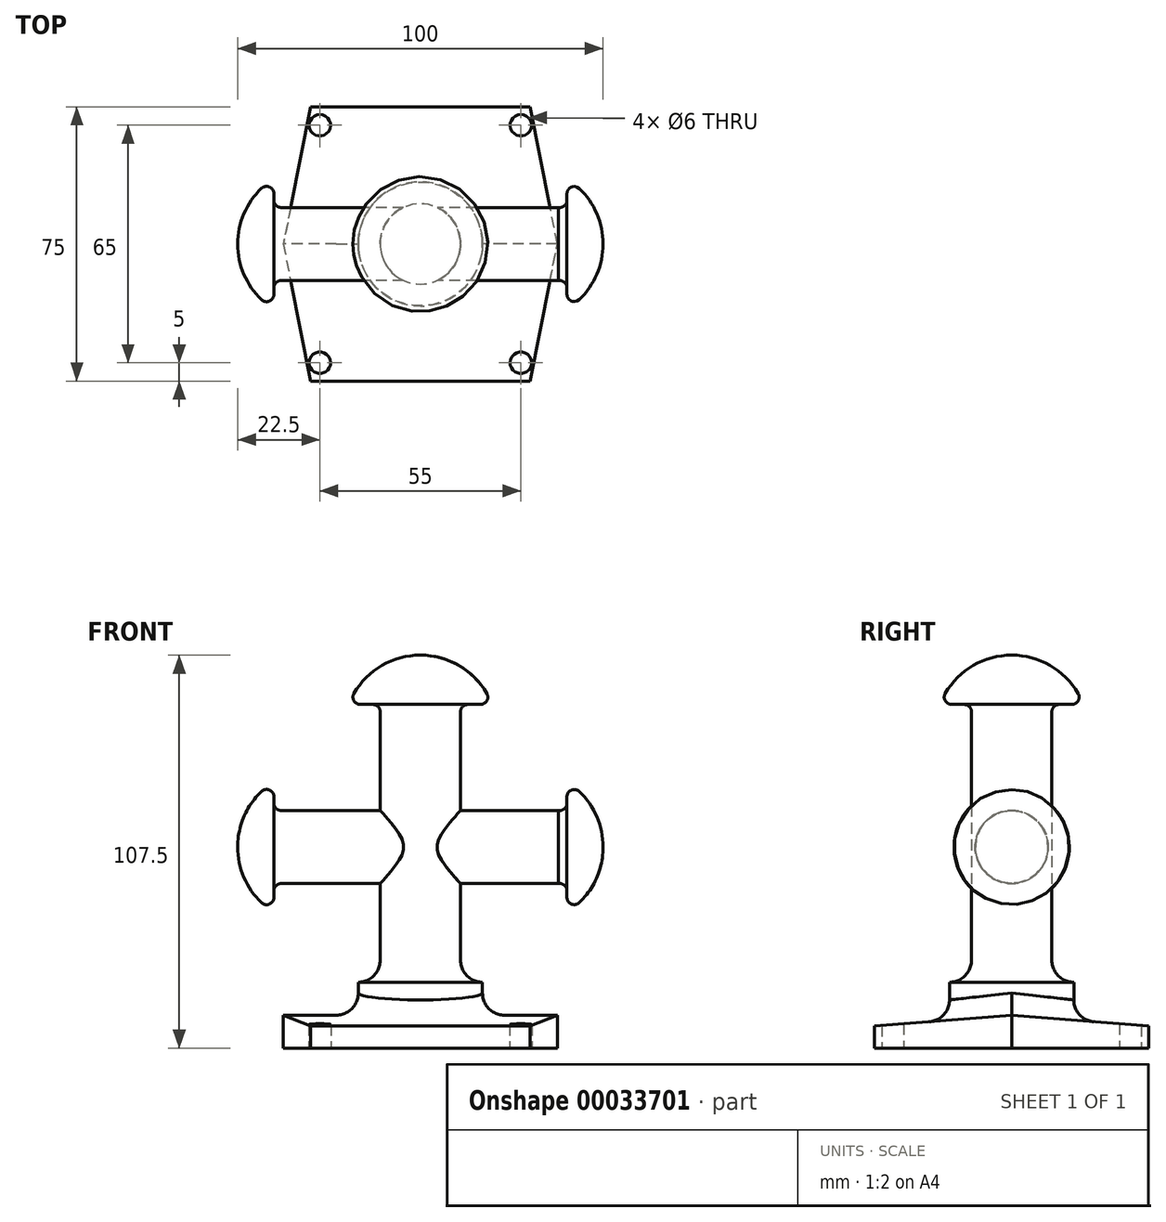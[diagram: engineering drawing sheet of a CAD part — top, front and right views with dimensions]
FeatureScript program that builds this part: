
annotation { "Feature Type Name" : "Feature", "Feature Type Description" : "" }
export const myFeature = defineFeature(function(context is Context, id is Id, definition is map)
    precondition{}
    {
        {
            var Q0;
            Q0=qCreatedBy(makeId("Front.planeOp"),FACE);
            var sketch = newSketch(context, id + "F0", { "sketchPlane" : qUnion([Q0])});
            skLineSegment(sketch, "E0", {"start": v(-38.09, 65) * mm, "end": v(37.8, 65) * mm});
            skLineSegment(sketch, "E1", {"start": v(-40.09, 67) * mm, "end": v(-40.09, 68.77) * mm});
            skArc(sketch, "E2", {"start": v(-43.47, 70.22) * mm, "mid": v(-48.3, 63.28) * mm, "end": v(-50, 55) * mm});
            skPoint(sketch, "E3.visualSharp", {"position": v(-40.09, 72.83) * mm});
            skArc(sketch, "E3.filletArc", {"start": v(-40.09, 68.77) * mm, "mid": v(-41.3, 70.61) * mm, "end": v(-43.47, 70.22) * mm});
            skPoint(sketch, "E4.visualSharp", {"position": v(-40.09, 65) * mm});
            skArc(sketch, "E4.filletArc", {"start": v(-40.09, 67) * mm, "mid": v(-39.5, 65.59) * mm, "end": v(-38.09, 65) * mm});
            skLineSegment(sketch, "E5", {"start": v(-29, 55) * mm, "end": v(29, 55) * mm});
            skLineSegment(sketch, "E6", {"start": v(0, 0) * mm, "end": v(0, 55) * mm, "construction": true});
            skArc(sketch, "E7", {"start": v(50, 55) * mm, "mid": v(48.3, 63.26) * mm, "end": v(43.5, 70.2) * mm});
            skArc(sketch, "E8", {"start": v(43.5, 70.2) * mm, "mid": v(41.33, 70.59) * mm, "end": v(40.12, 68.75) * mm});
            skLineSegment(sketch, "E9", {"start": v(40.12, 68.75) * mm, "end": v(40.12, 66.98) * mm});
            skArc(sketch, "E10", {"start": v(40.12, 66.98) * mm, "mid": v(39.41, 65.45) * mm, "end": v(37.8, 65) * mm});
            skLineSegment(sketch, "E11", {"start": v(-29, 55) * mm, "end": v(-50, 55) * mm});
            skLineSegment(sketch, "E12", {"start": v(29, 55) * mm, "end": v(50, 55) * mm});
            skSolve(sketch);
        }
        {
            var Q0;
            Q0 = qSketchRegion(id + "F0", true);
            var Q1;
            Q1=sQuery(id+"F0.wireOp",EDGE,"E5");
            revolve(context, id + "F1", {"entities" : qUnion([Q0]), "axis" : qUnion([Q1]), "revolveType" : RevolveType.FULL});
        }
        {
            var Q0;
            Q0=qCreatedBy(makeId("Front.planeOp"),FACE);
            var sketch = newSketch(context, id + "F2", { "sketchPlane" : qUnion([Q0])});
            skLineSegment(sketch, "E13", {"start": v(16.45, 94) * mm, "end": v(13, 94) * mm});
            skLineSegment(sketch, "E14", {"start": v(11, 92) * mm, "end": v(11, 18) * mm});
            skArc(sketch, "E15", {"start": v(18.19, 97) * mm, "mid": v(10.5, 104.69) * mm, "end": v(0, 107.5) * mm});
            skPoint(sketch, "E16.visualSharp", {"position": v(19.62, 94) * mm});
            skArc(sketch, "E16.filletArc", {"start": v(16.45, 94) * mm, "mid": v(18.19, 95) * mm, "end": v(18.19, 97) * mm});
            skPoint(sketch, "E17.visualSharp", {"position": v(11, 94) * mm});
            skArc(sketch, "E17.filletArc", {"start": v(13, 94) * mm, "mid": v(11.59, 93.41) * mm, "end": v(11, 92) * mm});
            skLineSegment(sketch, "E18", {"start": v(0, 0) * mm, "end": v(0, 107.5) * mm});
            skLineSegment(sketch, "E19", {"start": v(17, 18) * mm, "end": v(17, 0) * mm});
            skLineSegment(sketch, "E20", {"start": v(0, 0) * mm, "end": v(17, 0) * mm});
            skLineSegment(sketch, "E21.trimOffspring", {"start": v(11, 18) * mm, "end": v(17, 18) * mm});
            skSolve(sketch);
        }
        {
            var Q0;
            Q0 = qSketchRegion(id + "F2", true);
            var Q1;
            Q1=sQuery(id+"F2.wireOp",EDGE,"E18");
            revolve(context, id + "F3", {"operationType" : NewBodyOperationType.ADD, "entities" : qUnion([Q0]), "axis" : qUnion([Q1]), "revolveType" : RevolveType.FULL});
        }
        {
            var Q0;
            Q0=qCreatedBy(makeId("Right.planeOp"),FACE);
            var sketch = newSketch(context, id + "F4", { "sketchPlane" : qUnion([Q0])});
            skLineSegment(sketch, "E22.bottom", {"start": v(-37.5, 0) * mm, "end": v(37.5, 0) * mm});
            skLineSegment(sketch, "E22.left", {"start": v(-37.5, 0) * mm, "end": v(-37.5, 6) * mm});
            skLineSegment(sketch, "E22.right", {"start": v(37.5, 0) * mm, "end": v(37.5, 6) * mm});
            skLineSegment(sketch, "E23", {"start": v(-37.5, 6) * mm, "end": v(0, 9) * mm});
            skLineSegment(sketch, "E24", {"start": v(0, 9) * mm, "end": v(37.5, 6) * mm});
            skSolve(sketch);
        }
        {
            var Q0;
            Q0 = qSketchRegion(id + "F4", true);
            extrude(context, id + "F5", {"entities" : qUnion([Q0]), "operationType" : NewBodyOperationType.ADD, "endBound" : BoundingType.SYMMETRIC, "depth" : 75 * mm});
        }
        {
            var Q0;
            Q0=makeQuery(id+"F3.opRevolve","SWEPT_EDGE",EDGE,{"disambiguationData":[OSD([sQuery(id+"F2.wireOp",EDGE,"E14"),sQuery(id+"F2.wireOp",EDGE,"E21.trimOffspring")])]});
            var Q1;
            Q1=makeQuery(id+"F5.boolean.opBoolean","INTERSECT",EDGE,{"derivedFrom":[makeQuery(id+"F3.opRevolve","SWEPT_FACE",FACE,{"disambiguationData":[OSD([sQuery(id+"F2.wireOp",EDGE,"E19")])]}),makeQuery(id+"F5.opExtrude","SWEPT_FACE",FACE,{"disambiguationData":[OSD([sQuery(id+"F4.wireOp",EDGE,"E23")])]})]});
            var Q2;
            Q2=makeQuery(id+"F5.boolean.opBoolean","INTERSECT",EDGE,{"derivedFrom":[makeQuery(id+"F3.opRevolve","SWEPT_FACE",FACE,{"disambiguationData":[OSD([sQuery(id+"F2.wireOp",EDGE,"E19")])]}),makeQuery(id+"F5.opExtrude","SWEPT_FACE",FACE,{"disambiguationData":[OSD([sQuery(id+"F4.wireOp",EDGE,"E24")])]})]});
            fillet(context, id + "F6", {"entities" : qUnion([Q0, Q1, Q2]), "radius" : 6 * mm, "tangentPropagation" : true, "allowEdgeOverflow" : false});
        }
        {
            var Q0;
            Q0=qCreatedBy(makeId("Top.planeOp"),FACE);
            var sketch = newSketch(context, id + "F7", { "sketchPlane" : qUnion([Q0])});
            skCircle(sketch, "E25", {"center": v(-27.5, 32.5) * mm, "radius": 3 * mm});
            skCircle(sketch, "E26", {"center": v(27.5, 32.5) * mm, "radius": 3 * mm});
            skCircle(sketch, "E27", {"center": v(27.5, -32.5) * mm, "radius": 3 * mm});
            skCircle(sketch, "E28", {"center": v(-27.5, -32.5) * mm, "radius": 3 * mm});
            skLineSegment(sketch, "E29", {"start": v(-27.5, 32.5) * mm, "end": v(27.5, -32.5) * mm, "construction": true});
            skLineSegment(sketch, "E30", {"start": v(27.5, 32.5) * mm, "end": v(-27.5, -32.5) * mm, "construction": true});
            skSolve(sketch);
        }
        {
            var Q0;
            Q0 = qSketchRegion(id + "F7", true);
            extrude(context, id + "F8", {"entities" : qUnion([Q0]), "operationType" : NewBodyOperationType.REMOVE, "endBound" : BoundingType.UP_TO_NEXT, "depth" : 25 * mm});
        }
        {
            var Q0;
            Q0=qCreatedBy(makeId("Top.planeOp"),FACE);
            var sketch = newSketch(context, id + "F9", { "sketchPlane" : qUnion([Q0])});
            skLineSegment(sketch, "E31", {"start": v(-30, 37.5) * mm, "end": v(-37.5, 0) * mm});
            skLineSegment(sketch, "E32", {"start": v(-37.5, 0) * mm, "end": v(-30, -37.5) * mm});
            skLineSegment(sketch, "E33", {"start": v(-30, -37.5) * mm, "end": v(30, -37.5) * mm});
            skLineSegment(sketch, "E34", {"start": v(30, -37.5) * mm, "end": v(37.5, 0) * mm});
            skLineSegment(sketch, "E35", {"start": v(37.5, 0) * mm, "end": v(30, 37.5) * mm});
            skLineSegment(sketch, "E36", {"start": v(30, 37.5) * mm, "end": v(-30, 37.5) * mm});
            skPoint(sketch, "E37.visualSharp", {"position": v(-30, 37.5) * mm});
            skPoint(sketch, "E38.visualSharp", {"position": v(30, 37.5) * mm});
            skPoint(sketch, "E39.visualSharp", {"position": v(37.5, 0) * mm});
            skPoint(sketch, "E40.visualSharp", {"position": v(30, -37.5) * mm});
            skLineSegment(sketch, "E40.filletArc", {"start": v(30, -37.5) * mm, "end": v(30, -37.5) * mm});
            skPoint(sketch, "E41.visualSharp", {"position": v(-30, -37.5) * mm});
            skPoint(sketch, "E42.visualSharp", {"position": v(-37.5, 0) * mm});
            skLineSegment(sketch, "E43", {"start": v(0, 37.5) * mm, "end": v(0, -37.5) * mm, "construction": true});
            skLineSegment(sketch, "E44.bottom", {"start": v(-37.5, 37.5) * mm, "end": v(37.5, 37.5) * mm});
            skLineSegment(sketch, "E44.top", {"start": v(-37.5, -37.5) * mm, "end": v(37.5, -37.5) * mm});
            skLineSegment(sketch, "E44.left", {"start": v(-37.5, 37.5) * mm, "end": v(-37.5, -37.5) * mm});
            skLineSegment(sketch, "E44.right", {"start": v(37.5, 37.5) * mm, "end": v(37.5, -37.5) * mm});
            skSolve(sketch);
        }
        {
            var Q0;
            {var subQ3=sQuery(id+"F9.wireOp",EDGE,"E31");Q0=makeQuery(id+"F9.imprint","IMPRINT",FACE,{"disambiguationData":[TD([[makeQuery(id+"F9.imprint","IMPRINT",EDGE,{"derivedFrom":subQ3}),-1.0]])]});}
            var Q1;
            {var subQ3=sQuery(id+"F9.wireOp",EDGE,"E32");Q1=makeQuery(id+"F9.imprint","IMPRINT",FACE,{"disambiguationData":[TD([[makeQuery(id+"F9.imprint","IMPRINT",EDGE,{"derivedFrom":subQ3}),-1.0]])]});}
            var Q2;
            {var subQ3=sQuery(id+"F9.wireOp",EDGE,"E34");Q2=makeQuery(id+"F9.imprint","IMPRINT",FACE,{"disambiguationData":[TD([[makeQuery(id+"F9.imprint","IMPRINT",EDGE,{"derivedFrom":subQ3}),-1.0]])]});}
            var Q3;
            {var subQ3=sQuery(id+"F9.wireOp",EDGE,"E35");Q3=makeQuery(id+"F9.imprint","IMPRINT",FACE,{"disambiguationData":[TD([[makeQuery(id+"F9.imprint","IMPRINT",EDGE,{"derivedFrom":subQ3}),-1.0]])]});}
            extrude(context, id + "F10", {"entities" : qUnion([Q0, Q1, Q2, Q3]), "operationType" : NewBodyOperationType.REMOVE, "endBound" : BoundingType.UP_TO_NEXT, "depth" : 10 * mm});
        }
    });
